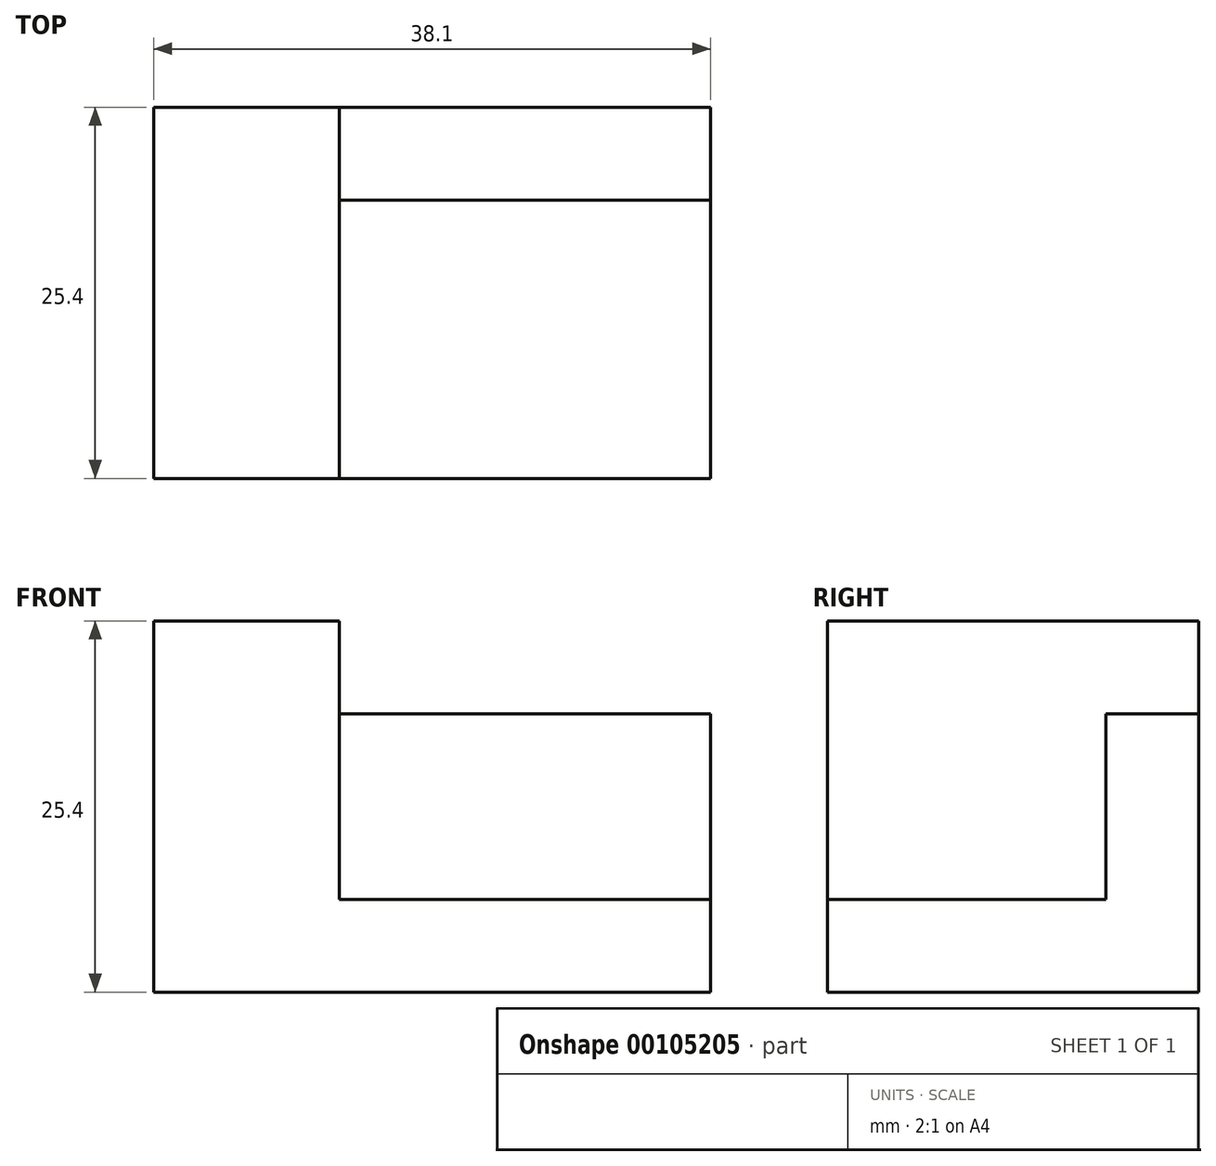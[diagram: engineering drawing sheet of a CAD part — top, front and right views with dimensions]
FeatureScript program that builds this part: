
annotation { "Feature Type Name" : "Feature", "Feature Type Description" : "" }
export const myFeature = defineFeature(function(context is Context, id is Id, definition is map)
    precondition{}
    {
        {
            var Q0;
            Q0=qCreatedBy(makeId("Front.planeOp"),FACE);
            var sketch = newSketch(context, id + "F0", { "sketchPlane" : qUnion([Q0])});
            skLineSegment(sketch, "E0", {"start": v(0, 0) * mm, "end": v(0, 25.4) * mm});
            skLineSegment(sketch, "E1", {"start": v(0, 25.4) * mm, "end": v(12.7, 25.4) * mm});
            skLineSegment(sketch, "E2", {"start": v(38.1, 0) * mm, "end": v(0, 0) * mm});
            skLineSegment(sketch, "E3", {"start": v(12.7, 6.35) * mm, "end": v(38.1, 6.35) * mm});
            skLineSegment(sketch, "E4", {"start": v(12.7, 25.4) * mm, "end": v(12.7, 6.35) * mm});
            skLineSegment(sketch, "E5", {"start": v(38.1, 6.35) * mm, "end": v(38.1, 0) * mm});
            skSolve(sketch);
        }
        {
            var Q0;
            Q0=makeQuery(id+"F0.imprint","IMPRINT",FACE,{"disambiguationData":[TD([[makeQuery(id+"F0.imprint","IMPRINT",EDGE,{"derivedFrom":sQuery(id+"F0.wireOp",EDGE,"E0")}),-1.0]])]});
            extrude(context, id + "F1", {"entities" : qUnion([Q0]), "depth" : 25.4 * mm});
        }
        {
            var Q0;
            Q0=qCreatedBy(makeId("Front.planeOp"),FACE);
            var sketch = newSketch(context, id + "F2", { "sketchPlane" : qUnion([Q0])});
            skLineSegment(sketch, "E6", {"start": v(12.7, 6.35) * mm, "end": v(38.1, 6.35) * mm});
            skLineSegment(sketch, "E7", {"start": v(38.1, 6.35) * mm, "end": v(38.1, 19.05) * mm});
            skLineSegment(sketch, "E8", {"start": v(38.1, 19.05) * mm, "end": v(12.7, 19.05) * mm});
            skLineSegment(sketch, "E9", {"start": v(12.7, 19.05) * mm, "end": v(12.7, 6.35) * mm});
            skSolve(sketch);
        }
        {
            var Q0;
            Q0 = qSketchRegion(id + "F2", true);
            extrude(context, id + "F3", {"entities" : qUnion([Q0]), "operationType" : NewBodyOperationType.ADD, "depth" : 6.35 * mm});
        }
    });
